# Revit family: leddownlightrc-p-mw_r200-23w-4000_140057173
name_source: partatom
category: Leuchten
revit_build: Autodesk Revit 2016 (Build: 20190508_0715(x64)
units: mm (PartAtom-declared; Revit-internal decimal feet)

## family parameters
Basisbauteil = Fläche
Beim Laden mit Abzugskörper schneiden = Nein
Bemaßung runder Anschluss = Durchmesser verwenden
Gemeinsam genutzt = Nein
Lichtquelle = Nein
Raumberechnungspunkt = Nein
Teiletyp = Normal

## types (1)
- LEDDownlightRc-P-MW R200-23W-4000 (1 x LED, 2530 lm)
    Approval mark = CE, ENEC
    Beschreibung = Advanced high quality LED downlight. Unique optical lens concept with matte white (MW) reflector and low glare. Direct replacement for compact fluorescent downlights - saving over 60% of energy costs. IP44 on light emitting side. Provided with protective foil in order to protect the optics against dust and dirt during the installation.
    CIE Flux Codes = 82 97 99 100 100
    Control Gear = Electronic ballast
    Height = 0 mm  [stored 0 ft]
    Hersteller = OPPLE
    Lamp Light Flux = 2530 lm
    Lamp count = 1
    Lampe = 1 x LED
    Length = 225 mm
    Luminous efficacy = 110 lm/W
    ModVariant = Nein
    Modell = 140057173
    Mounting Place = Ceiling
    Mounting Type = Surface mounted, Recessed
    Number of Poles = 1
    OnlyDefault = Ja
    Power Factor = 1
    Product Name = LEDDownlightRc-P-MW R200-23W-4000
    Product group = Downlight Performer MW
    ProductGroupID = 404
    Protection Class = Protection class II
    Protection Degree = IP 44
    RLX_Detail_Level = 1
    RlxData = <blob elided: 174893 chars, md5=029491c5>
    Scheinlast = 23 VA
    Socket = socket
    Standby Power = 0 W
    System Light Flux = 2530 lm
    System Power = 23 W
    Typenbild = 140057173.jpg
    Typenkommentare = Product without accessories
    URL = http://relux.com
    VarID = ---
    Voltage = 0 V
    Vorgabe-Ansicht = 1800 mm
    Weight = 0.00 kg
    Width = 0 mm  [stored 0 ft]

note: [stored X ft] marks values corroborated as IEEE doubles in the binary element streams (Revit-internal decimal feet)

## geometry (parser evidence)
native form markers: Sweep x9
no freeform markers — native parametric forms only
